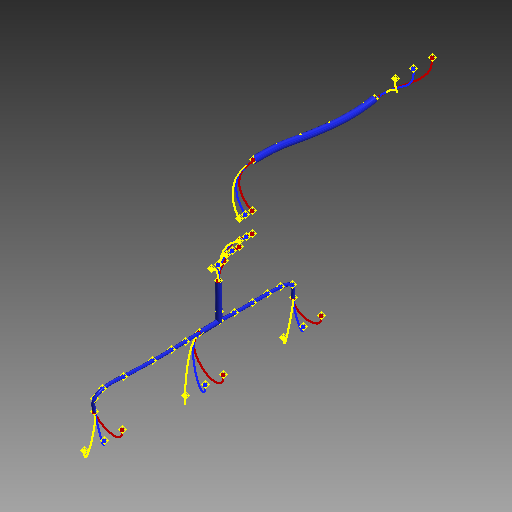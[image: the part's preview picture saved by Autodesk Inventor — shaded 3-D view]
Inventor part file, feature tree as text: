
AUTODESK INVENTOR PART (.ipt)
format: ipt  version: 2017 (Build 210142000, 142)  size: 326,144 bytes
history: native  units: mm (DEFAULTED — no unit token found)
features: other x69, plane x5, sketch x5, sweep x5
ambient origin geometry x8: Origin, YZ Plane, XZ Plane, XY Plane, X Axis, Y Axis, Z Axis, Center Point
bodies: Body1 (feature_tree), Body2 (feature_tree), Body3 (feature_tree), Body4 (feature_tree), Body5 (feature_tree)
feature tree (84):
  other  "Work Point1"
  other  "Work Point2"
  other  "Wire1"
  other  "Work Point3"
  other  "Work Point4"
  other  "Wire2"
  other  "Work Point5"
  other  "Work Point6"
  other  "Wire3"
  other  "Work Point7"
  other  "Work Point8"
  other  "Wire4"
  other  "Work Point9"
  other  "Work Point10"
  other  "Wire5"
  other  "Work Point11"
  other  "Work Point12"
  other  "Wire6"
  other  "Work Point13"
  other  "Work Point14"
  other  "Wire7"
  other  "Work Point15"
  other  "Work Point16"
  other  "Wire8"
  other  "Work Point17"
  other  "Work Point18"
  other  "Wire9"
  other  "Work Point19"
  other  "Work Point20"
  other  "Wire10"
  other  "Work Point21"
  other  "Work Point22"
  other  "Wire11"
  other  "Work Point23"
  other  "Work Point24"
  other  "Wire12"
  other  "Work Point25"
  other  "Work Point26"
  other  "Segment1"
  other  "Work Point27"
  other  "Work Point28"
  other  "Work Point29"
  other  "Work Point30"
  plane  "Work Plane1"
  other  "Work Point31"
  other  "Work Point32"
  other  "Segment2"
  other  "Work Point33"
  plane  "Work Plane2"
  other  "Work Point34"
  other  "Segment3"
  plane  "Work Plane3"
  other  "Work Point35"
  other  "Segment4"
  other  "Work Point36"
  other  "Work Point37"
  other  "Work Point38"
  other  "Work Point39"
  other  "Work Point40"
  other  "Work Point41"
  plane  "Work Plane4"
  other  "Work Point42"
  other  "Segment5"
  other  "Work Point43"
  other  "Work Point44"
  other  "Work Point45"
  other  "Work Point46"
  other  "Work Point47"
  plane  "Work Plane5"
  sketch  "Sketch1"  dims[d0=0.0mm d1=0.0mm d2=0.0mm d3=0.0mm]
  other  "Srf1"
  sketch  "Sketch2"  dims[d4=0.0mm d5=0.0mm d6=0.0mm d7=0.0mm]
  other  "Srf2"
  sketch  "Sketch3"  dims[d8=0.0mm d9=0.0mm]
  other  "Srf3"
  sketch  "Sketch4"
  other  "Srf4"
  sketch  "Sketch5"
  other  "Srf5"
  sweep  "SweepSrf1"
  sweep  "SweepSrf2"
  sweep  "SweepSrf3"
  sweep  "SweepSrf4"
  sweep  "SweepSrf5"
